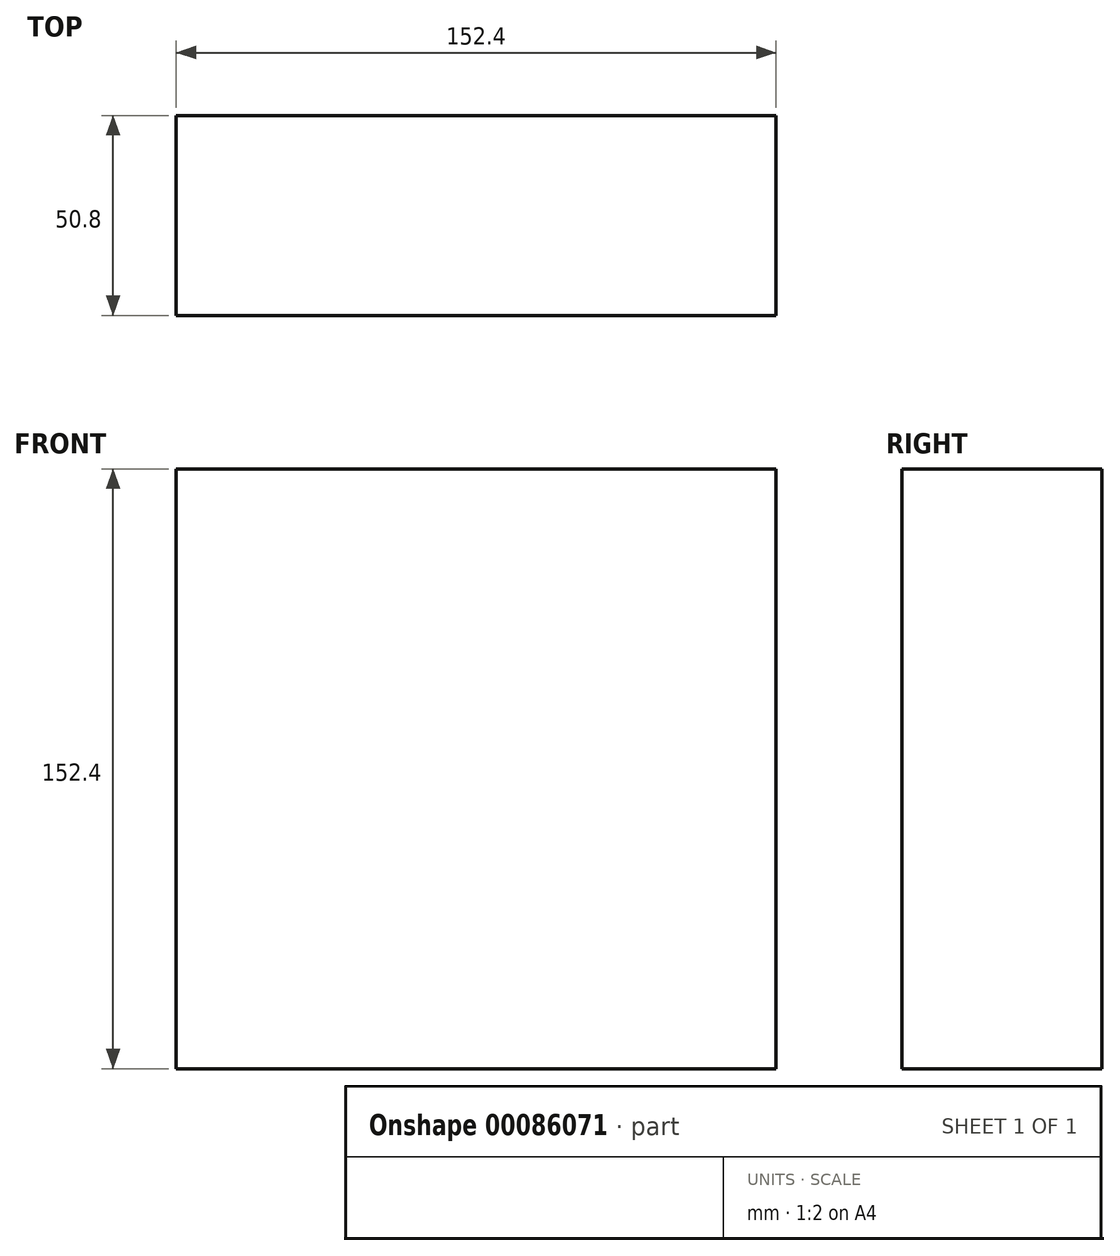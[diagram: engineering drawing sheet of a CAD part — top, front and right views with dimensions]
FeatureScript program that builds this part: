
annotation { "Feature Type Name" : "Feature", "Feature Type Description" : "" }
export const myFeature = defineFeature(function(context is Context, id is Id, definition is map)
    precondition{}
    {
        {
            var Q0;
            Q0=qCreatedBy(makeId("Front.planeOp"),FACE);
            var sketch = newSketch(context, id + "F0", { "sketchPlane" : qUnion([Q0])});
            skLineSegment(sketch, "E0.bottom", {"start": v(-99.1, -48.8) * mm, "end": v(53.3, -48.8) * mm});
            skLineSegment(sketch, "E0.top", {"start": v(-99.1, 103.6) * mm, "end": v(53.3, 103.6) * mm});
            skLineSegment(sketch, "E0.left", {"start": v(-99.1, -48.8) * mm, "end": v(-99.1, 103.6) * mm});
            skLineSegment(sketch, "E0.right", {"start": v(53.3, -48.8) * mm, "end": v(53.3, 103.6) * mm});
            skLineSegment(sketch, "E1", {"start": v(-22.9, 103.6) * mm, "end": v(-99.1, 27.4) * mm});
            skSolve(sketch);
        }
        {
            var Q0;
            {var subQ3=sQuery(id+"F0.wireOp",EDGE,"E1");Q0=makeQuery(id+"F0.imprint","IMPRINT",FACE,{"disambiguationData":[TD([[makeQuery(id+"F0.imprint","IMPRINT",EDGE,{"derivedFrom":subQ3}),-1.0]])]});}
            var Q1;
            {var subQ2=sQuery(id+"F0.wireOp",EDGE,"E0.bottom");Q1=makeQuery(id+"F0.imprint","IMPRINT",FACE,{"disambiguationData":[TD([[makeQuery(id+"F0.imprint","IMPRINT",EDGE,{"derivedFrom":subQ2}),1.0]])]});}
            extrude(context, id + "F1", {"entities" : qUnion([Q0, Q1]), "endBound" : BoundingType.SYMMETRIC, "depth" : 50.8 * mm});
        }
    });
